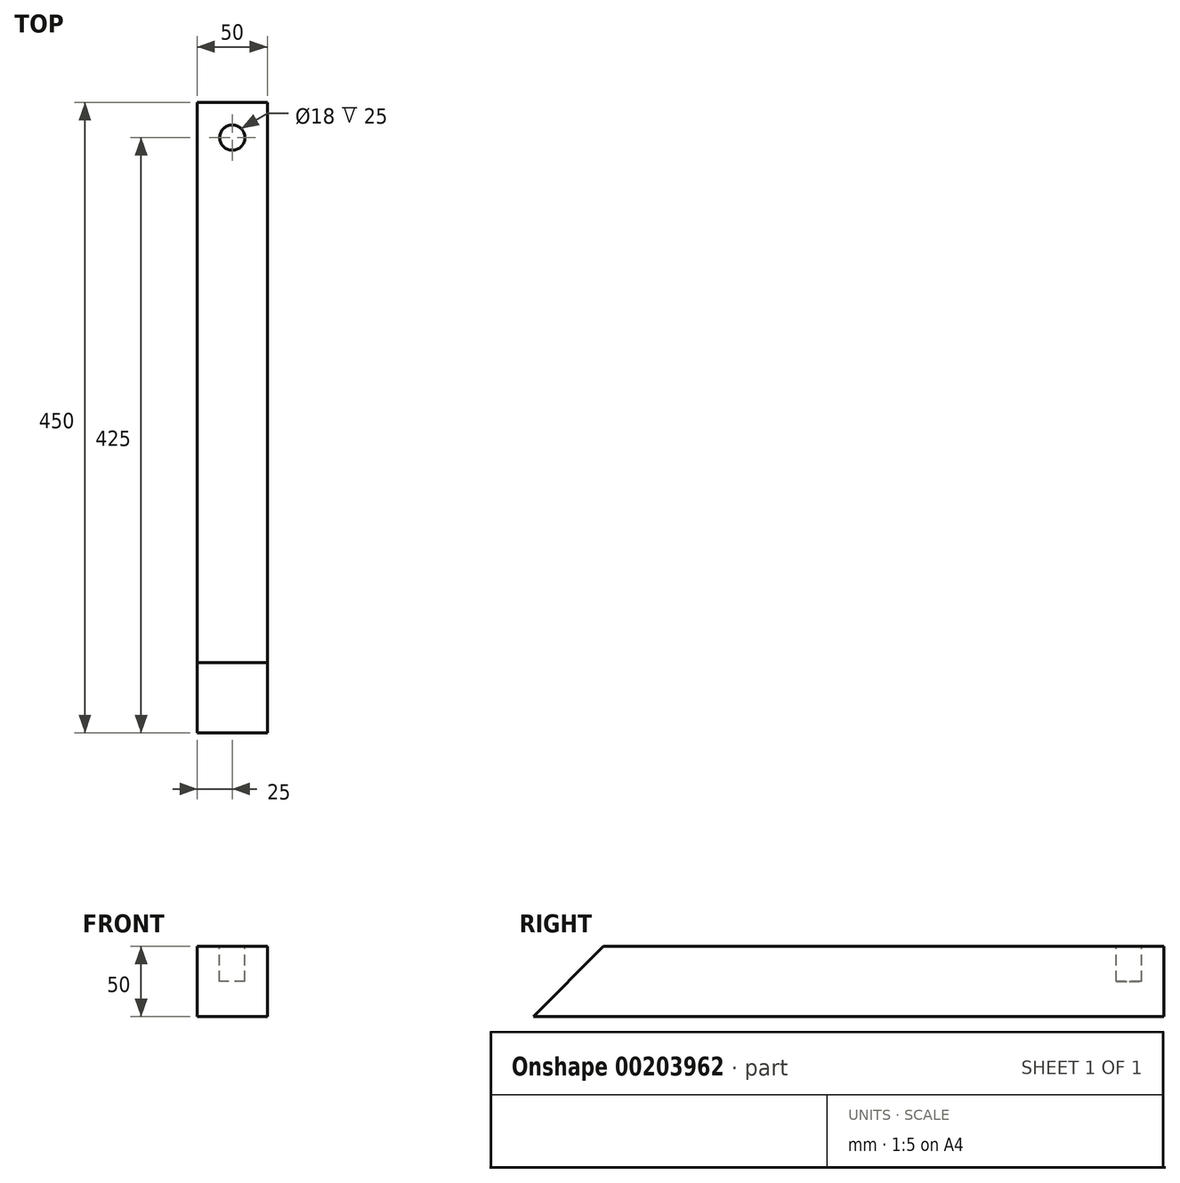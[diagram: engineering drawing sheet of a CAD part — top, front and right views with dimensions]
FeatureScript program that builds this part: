
annotation { "Feature Type Name" : "Feature", "Feature Type Description" : "" }
export const myFeature = defineFeature(function(context is Context, id is Id, definition is map)
    precondition{}
    {
        {
            var Q0;
            Q0=qCreatedBy(makeId("Front.planeOp"),FACE);
            var sketch = newSketch(context, id + "F0", { "sketchPlane" : qUnion([Q0])});
            skLineSegment(sketch, "E0.bottom", {"start": v(25, -25) * mm, "end": v(-25, -25) * mm});
            skLineSegment(sketch, "E0.top", {"start": v(25, 25) * mm, "end": v(-25, 25) * mm});
            skLineSegment(sketch, "E0.left", {"start": v(25, -25) * mm, "end": v(25, 25) * mm});
            skLineSegment(sketch, "E0.right", {"start": v(-25, -25) * mm, "end": v(-25, 25) * mm});
            skPoint(sketch, "E0.middle", {"position": v(0, 0) * mm});
            skSolve(sketch);
        }
        {
            var Q0;
            Q0=qSketchRegion(id+"F0",true);
            extrude(context, id + "F1", {"entities" : qUnion([Q0]), "depth" : 450 * mm});
        }
        {
            var Q0;
            Q0=makeQuery(id+"F1.opExtrude","SWEPT_FACE",FACE,{"disambiguationData":[OSD([sQuery(id+"F0.wireOp",EDGE,"E0.left")])]});
            var sketch = newSketch(context, id + "F2", { "sketchPlane" : qUnion([Q0])});
            skLineSegment(sketch, "E1", {"start": v(-450, 25) * mm, "end": v(-400, 25) * mm});
            skLineSegment(sketch, "E2", {"start": v(-400, 25) * mm, "end": v(-450, -25) * mm});
            skLineSegment(sketch, "E3", {"start": v(-450, -25) * mm, "end": v(-450, 25) * mm});
            skSolve(sketch);
        }
        {
            var Q0;
            Q0 = qSketchRegion(id + "F2", true);
            extrude(context, id + "F3", {"entities" : qUnion([Q0]), "operationType" : NewBodyOperationType.REMOVE, "endBound" : BoundingType.THROUGH_ALL, "oppositeDirection" : true, "depth" : 25 * mm});
        }
        {
            var Q0;
            Q0=makeQuery(id+"F1.opExtrude","SWEPT_FACE",FACE,{"disambiguationData":[OSD([sQuery(id+"F0.wireOp",EDGE,"E0.top")])]});
            var sketch = newSketch(context, id + "F4", { "sketchPlane" : qUnion([Q0])});
            skLineSegment(sketch, "E4", {"start": v(0, 0) * mm, "end": v(0, -400) * mm, "construction": true});
            skCircle(sketch, "E5", {"center": v(0, -25) * mm, "radius": 9 * mm});
            skSolve(sketch);
        }
        {
            var Q0;
            Q0 = qSketchRegion(id + "F4", true);
            extrude(context, id + "F5", {"entities" : qUnion([Q0]), "operationType" : NewBodyOperationType.REMOVE, "oppositeDirection" : true, "depth" : 25 * mm});
        }
    });
